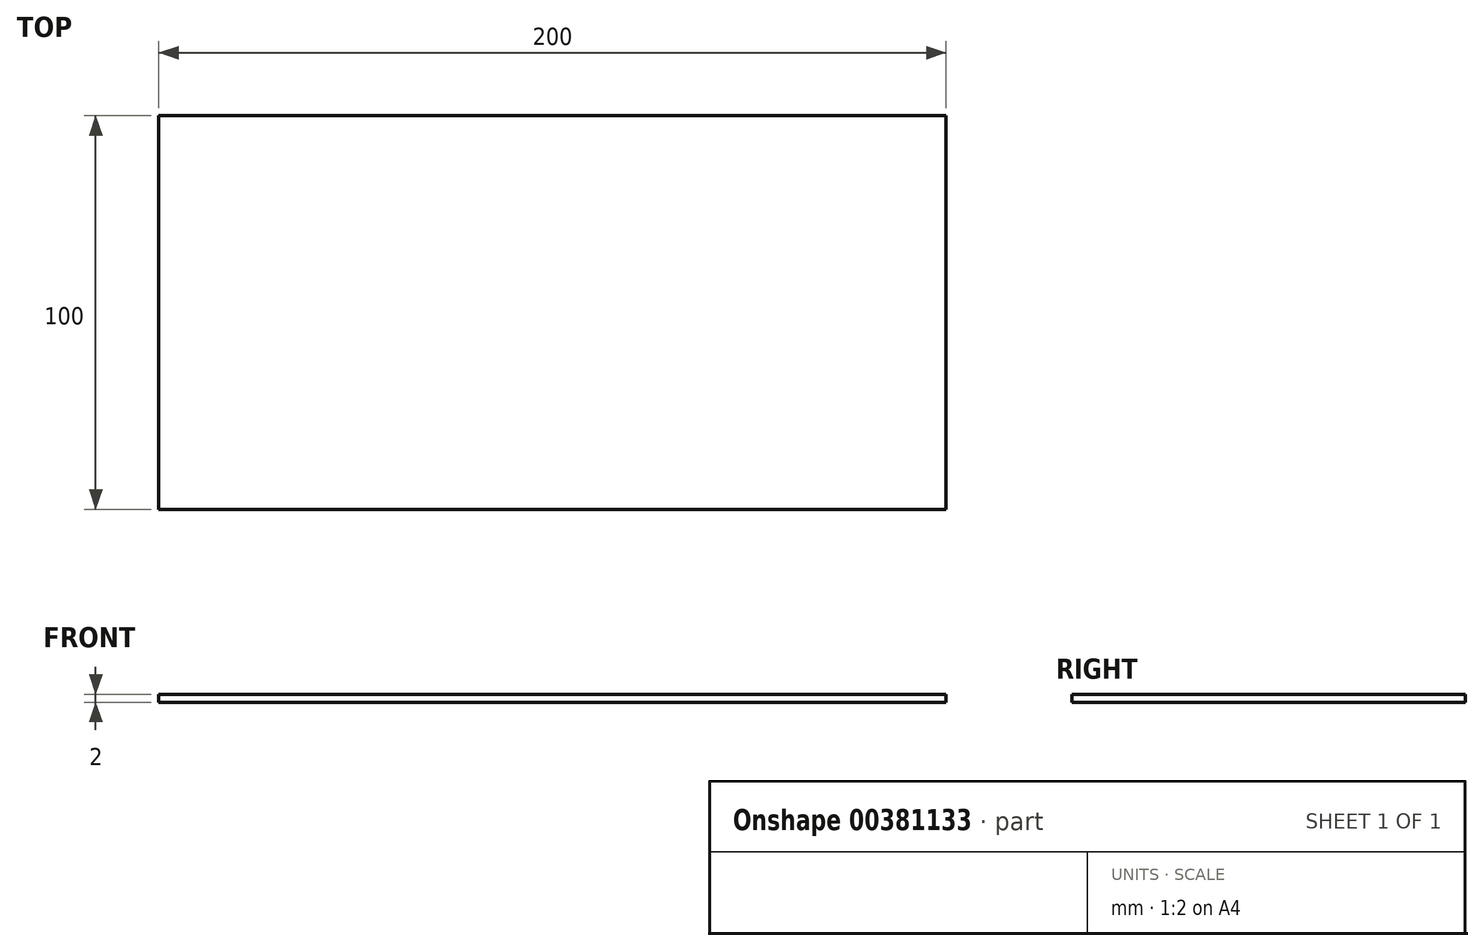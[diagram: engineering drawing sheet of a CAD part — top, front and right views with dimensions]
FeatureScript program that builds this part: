
annotation { "Feature Type Name" : "Feature", "Feature Type Description" : "" }
export const myFeature = defineFeature(function(context is Context, id is Id, definition is map)
    precondition{}
    {
        {
            var Q0;
            Q0=qCreatedBy(makeId("Top.planeOp"),FACE);
            var sketch = newSketch(context, id + "F0", { "sketchPlane" : qUnion([Q0])});
            skLineSegment(sketch, "E0.bottom", {"start": v(100, -50) * mm, "end": v(-100, -50) * mm});
            skLineSegment(sketch, "E0.top", {"start": v(100, 50) * mm, "end": v(-100, 50) * mm});
            skLineSegment(sketch, "E0.left", {"start": v(100, -50) * mm, "end": v(100, 50) * mm});
            skLineSegment(sketch, "E0.right", {"start": v(-100, -50) * mm, "end": v(-100, 50) * mm});
            skPoint(sketch, "E0.middle", {"position": v(0, 0) * mm});
            skSolve(sketch);
        }
        {
            var Q0;
            Q0 = qSketchRegion(id + "F0", true);
            extrude(context, id + "F1", {"entities" : qUnion([Q0]), "depth" : 2 * mm});
        }
    });
